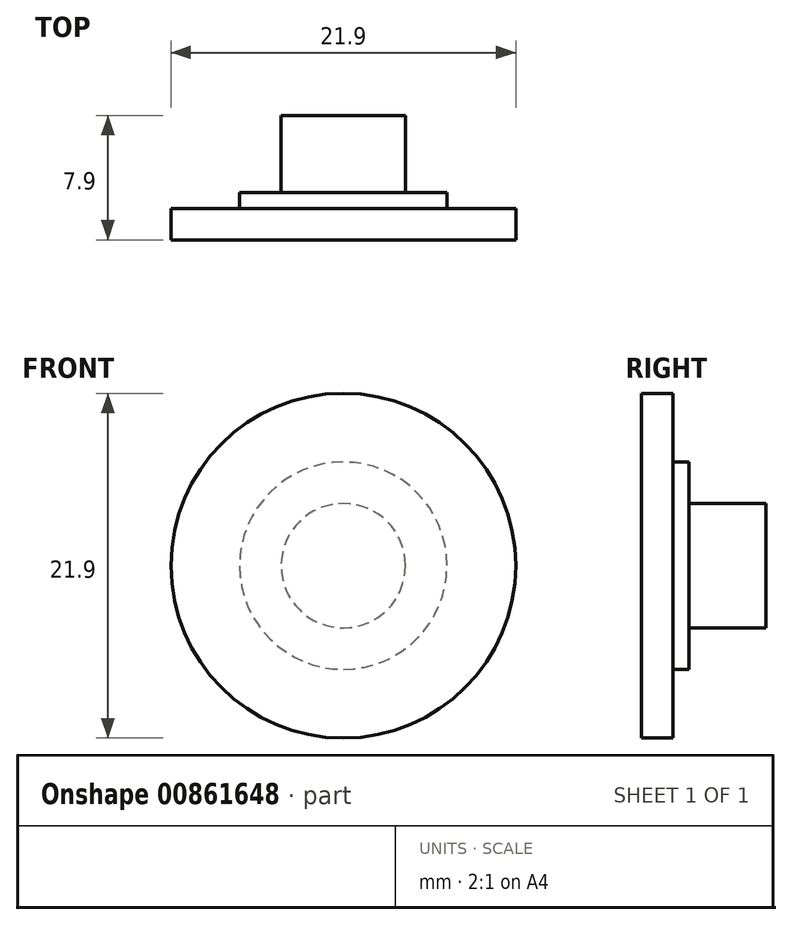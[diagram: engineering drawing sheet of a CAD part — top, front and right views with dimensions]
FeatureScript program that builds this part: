
annotation { "Feature Type Name" : "Feature", "Feature Type Description" : "" }
export const myFeature = defineFeature(function(context is Context, id is Id, definition is map)
    precondition{}
    {
        {
            var Q0;
            Q0=qCreatedBy(makeId("Top.planeOp"),FACE);
            var sketch = newSketch(context, id + "F0", { "sketchPlane" : qUnion([Q0])});
            skLineSegment(sketch, "E0", {"start": v(0, 7.9) * mm, "end": v(0, 0) * mm});
            skLineSegment(sketch, "E1", {"start": v(0, 0) * mm, "end": v(10.95, 0) * mm});
            skLineSegment(sketch, "E2", {"start": v(10.95, 0) * mm, "end": v(10.95, 2) * mm});
            skLineSegment(sketch, "E3", {"start": v(3.95, 7.9) * mm, "end": v(0, 7.9) * mm});
            skLineSegment(sketch, "E4", {"start": v(3.95, 7.9) * mm, "end": v(3.95, 3) * mm});
            skLineSegment(sketch, "E5", {"start": v(85.36, 16.72) * mm, "end": v(84.04, 16.72) * mm});
            skLineSegment(sketch, "E6.right", {"start": v(6.59, 3) * mm, "end": v(6.59, 2) * mm});
            skLineSegment(sketch, "E7", {"start": v(6.59, 2) * mm, "end": v(10.95, 2) * mm});
            skLineSegment(sketch, "E8", {"start": v(3.95, 3) * mm, "end": v(6.59, 3) * mm});
            skSolve(sketch);
        }
        {
            var Q0;
            Q0 = qSketchRegion(id + "F0", true);
            var Q1;
            Q1=sQuery(id+"F0.wireOp",EDGE,"E0");
            revolve(context, id + "F1", {"surfaceOperationType" : NewSurfaceOperationType.NEW, "entities" : qUnion([Q0]), "axis" : qUnion([Q1]), "revolveType" : RevolveType.FULL});
        }
    });
